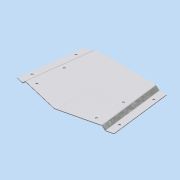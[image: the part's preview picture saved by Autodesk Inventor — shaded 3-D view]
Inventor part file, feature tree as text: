
AUTODESK INVENTOR PART (.ipt)
format: ipt  version: 2015 (Build 190159000, 159)  size: 164,352 bytes
history: native  units: in
note: dims shown in document units (in); Inventor stores cm internally (conversion verified against a paired STEP export)
features: sheet_metal_op x5, sketch x4, extrude x2, other x2, projected_geometry x2, plane x1, mirror x1
ambient origin geometry x8: Origin, YZ Plane, XZ Plane, XY Plane, X Axis, Y Axis, Z Axis, Center Point
bodies: Solid1 (feature_tree)
feature tree (17):
  sketch  "Sketch1"  dims[d0=5.5in d2=7.5in]
  sheet_metal_op  "Face1"
  plane  "Work Plane1"
  sheet_metal_op  "Face2"
  sheet_metal_op  "Bend2"
  sheet_metal_op  "Bend3"
  extrude  "Extrusion1"  Depth=7.5in
  extrude  "Extrusion2"  Depth=0.0625in
  mirror  "Mirror1"
  other  "Plate1"
  sketch  "Sketch2"  dims[d3=1.0in d4=0.0625in]
  other  "Plate2"
  sheet_metal_op  "Bend1"
  sketch  "Sketch3"  dims[d5=0.315in]
  projected_geometry  "Projected Loop1"
  projected_geometry  "Projected Loop2"
  sketch  "Sketch4"  dims[d6=0.0625in d7=0.0625in d8=0.0312in d9=0.125in d10=0.0625in d11=0.0625in d12=0.0312in d13=0.125in d14=0.0625in d15=0.0625in d16=0.0625in d17=0.0312in d18=0.125in d19=0.0625in d20=0.0625in d21=0.201in d22=0.201in d24=1.0in d25=1.0in d26=1.0in d27=0.0in d28=0.201in d29=0.201in d31=2.5in d32=0.0in d33=0.0in]
